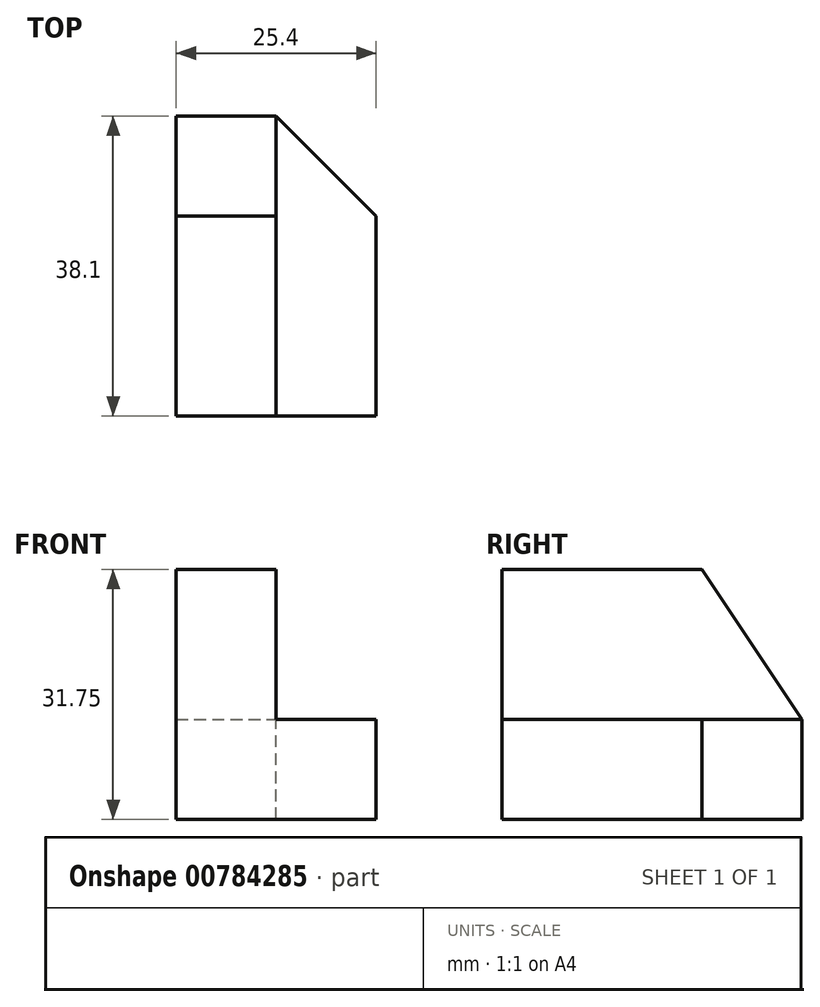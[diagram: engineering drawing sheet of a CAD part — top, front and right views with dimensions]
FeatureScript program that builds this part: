
annotation { "Feature Type Name" : "Feature", "Feature Type Description" : "" }
export const myFeature = defineFeature(function(context is Context, id is Id, definition is map)
    precondition{}
    {
        {
            var Q0;
            Q0=qCreatedBy(makeId("Front.planeOp"),FACE);
            var sketch = newSketch(context, id + "F0", { "sketchPlane" : qUnion([Q0])});
            skLineSegment(sketch, "E0", {"start": v(0, 0) * mm, "end": v(0, 31.75) * mm});
            skLineSegment(sketch, "E1", {"start": v(0, 31.75) * mm, "end": v(12.7, 31.75) * mm});
            skLineSegment(sketch, "E2", {"start": v(12.7, 31.75) * mm, "end": v(12.7, 12.7) * mm});
            skLineSegment(sketch, "E3", {"start": v(12.7, 12.7) * mm, "end": v(25.4, 12.7) * mm});
            skLineSegment(sketch, "E4", {"start": v(25.4, 12.7) * mm, "end": v(25.4, 0) * mm});
            skLineSegment(sketch, "E5", {"start": v(25.4, 0) * mm, "end": v(0, 0) * mm});
            skSolve(sketch);
        }
        {
            var Q0;
            Q0 = qSketchRegion(id + "F0", true);
            extrude(context, id + "F1", {"entities" : qUnion([Q0]), "depth" : 25.4 * mm, "offsetDistance" : 25.4 * mm});
        }
        {
            var Q0;
            Q0=makeQuery(id+"F1.opExtrude","CAP_FACE",FACE,{"disambiguationData":[OSD([sQuery(id+"F0.wireOp",EDGE,"E0"),sQuery(id+"F0.wireOp",EDGE,"E1"),sQuery(id+"F0.wireOp",EDGE,"E2"),sQuery(id+"F0.wireOp",EDGE,"E3"),sQuery(id+"F0.wireOp",EDGE,"E4"),sQuery(id+"F0.wireOp",EDGE,"E5")])],"isStart":true});
            extrude(context, id + "F2", {"entities" : qUnion([Q0]), "operationType" : NewBodyOperationType.ADD, "depth" : 12.7 * mm, "offsetDistance" : 25.4 * mm});
        }
        {
            var Q0;
            {var subQ0=sQuery(id+"F0.wireOp",EDGE,"E2");Q0=makeQuery(id+"F2.boolean.opBoolean","MERGE",FACE,{"derivedFrom":[makeQuery(id+"F1.opExtrude","SWEPT_FACE",FACE,{"disambiguationData":[OSD([subQ0])]}),makeQuery(id+"F2.opExtrude","SWEPT_FACE",FACE,{"disambiguationData":[OSD([subQ0])]})]});}
            var sketch = newSketch(context, id + "F3", { "sketchPlane" : qUnion([Q0])});
            skLineSegment(sketch, "E6", {"start": v(0, 31.75) * mm, "end": v(12.7, 12.7) * mm});
            skSolve(sketch);
        }
        {
            var Q0;
            {var subQ0=sQuery(id+"F3.wireOp",EDGE,"E6");Q0=makeQuery(id+"F3.imprint","IMPRINT",FACE,{"disambiguationData":[TD([[makeQuery(id+"F3.imprint","IMPRINT",EDGE,{"derivedFrom":subQ0}),1.0]])]});}
            extrude(context, id + "F4", {"entities" : qUnion([Q0]), "operationType" : NewBodyOperationType.REMOVE, "oppositeDirection" : true, "depth" : 25.4 * mm, "offsetDistance" : 25.4 * mm});
        }
        {
            var Q0;
            {var subQ0=sQuery(id+"F0.wireOp",EDGE,"E3");Q0=makeQuery(id+"F2.boolean.opBoolean","MERGE",FACE,{"derivedFrom":[makeQuery(id+"F1.opExtrude","SWEPT_FACE",FACE,{"disambiguationData":[OSD([subQ0])]}),makeQuery(id+"F2.opExtrude","SWEPT_FACE",FACE,{"disambiguationData":[OSD([subQ0])]})]});}
            var sketch = newSketch(context, id + "F5", { "sketchPlane" : qUnion([Q0])});
            skLineSegment(sketch, "E7", {"start": v(25.4, -25.4) * mm, "end": v(25.4, 0) * mm});
            skLineSegment(sketch, "E8", {"start": v(25.4, 0) * mm, "end": v(12.7, 12.7) * mm});
            skSolve(sketch);
        }
        {
            var Q0;
            {var subQ0=sQuery(id+"F5.wireOp",EDGE,"E8");Q0=makeQuery(id+"F5.imprint","IMPRINT",FACE,{"disambiguationData":[TD([[makeQuery(id+"F5.imprint","IMPRINT",EDGE,{"derivedFrom":subQ0}),-1.0]])]});}
            extrude(context, id + "F6", {"entities" : qUnion([Q0]), "operationType" : NewBodyOperationType.REMOVE, "oppositeDirection" : true, "depth" : 25.4 * mm, "offsetDistance" : 25.4 * mm});
        }
    });
